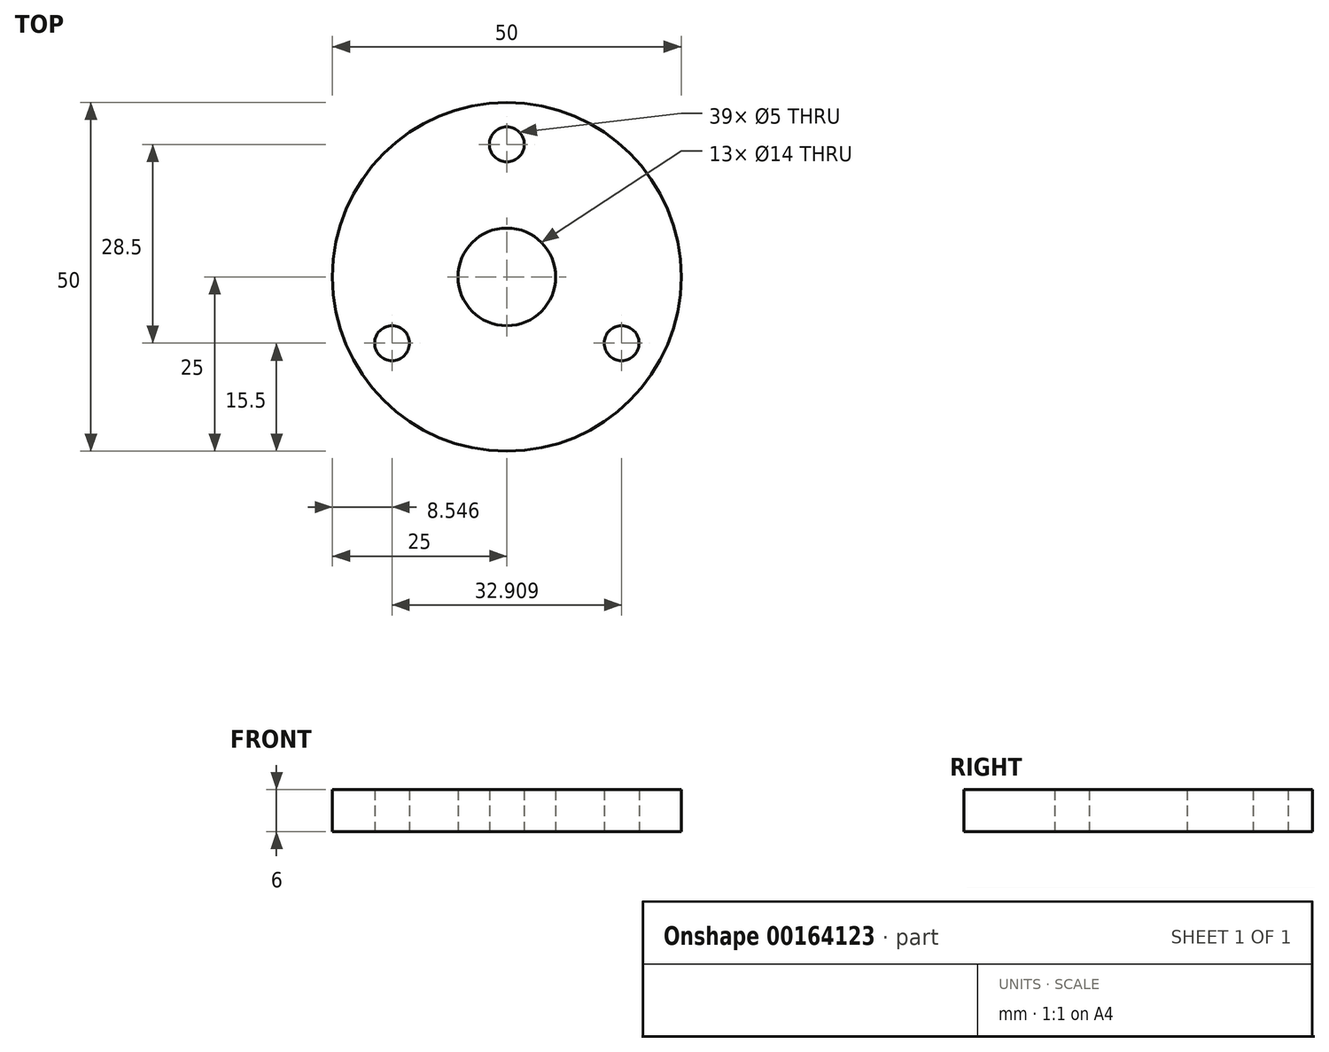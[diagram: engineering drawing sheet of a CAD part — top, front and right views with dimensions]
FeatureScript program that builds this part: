
annotation { "Feature Type Name" : "Feature", "Feature Type Description" : "" }
export const myFeature = defineFeature(function(context is Context, id is Id, definition is map)
    precondition{}
    {
        {
            var Q0;
            Q0=qCreatedBy(makeId("Top.planeOp"),FACE);
            var sketch = newSketch(context, id + "F0", { "sketchPlane" : qUnion([Q0])});
            skCircle(sketch, "E0", {"center": v(0, 0) * mm, "radius": 7 * mm});
            skCircle(sketch, "E1", {"center": v(0, 0) * mm, "radius": 25 * mm});
            skCircle(sketch, "E2", {"center": v(0, 19) * mm, "radius": 2.5 * mm});
            skCircle(sketch, "E3.1.0", {"center": v(-16.45, -9.5) * mm, "radius": 2.5 * mm});
            skCircle(sketch, "E3.2.0", {"center": v(16.45, -9.5) * mm, "radius": 2.5 * mm});
            skSolve(sketch);
        }
        {
            var Q0;
            Q0=makeQuery(id+"F0.imprint","IMPRINT",FACE,{"disambiguationData":[TD([[makeQuery(id+"F0.imprint","IMPRINT",EDGE,{"derivedFrom":sQuery(id+"F0.wireOp",EDGE,"E0")}),-1.0]])]});
            extrude(context, id + "F1", {"entities" : qUnion([Q0]), "depth" : 6 * mm});
        }
    });
